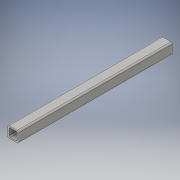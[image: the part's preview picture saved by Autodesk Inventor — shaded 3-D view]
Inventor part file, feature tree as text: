
AUTODESK INVENTOR PART (.ipt)
format: ipt  version: 2016 (Build 200138000, 138)  size: 113,664 bytes
history: native  units: in
note: dims shown in document units (in); Inventor stores cm internally (conversion verified against a paired STEP export)
features: extrude x1, sketch x1
ambient origin geometry x8: Origin, YZ Plane, XZ Plane, XY Plane, X Axis, Y Axis, Z Axis, Center Point
bodies: Solid1 (feature_tree)
feature tree (2):
  extrude  "Extrusion1"  Depth=1.0in
  sketch  "Sketch1"  dims[d0=1.0in d1=1.0in d2=0.125in d3=0.125in d4=14.0in d5=0.0in]
